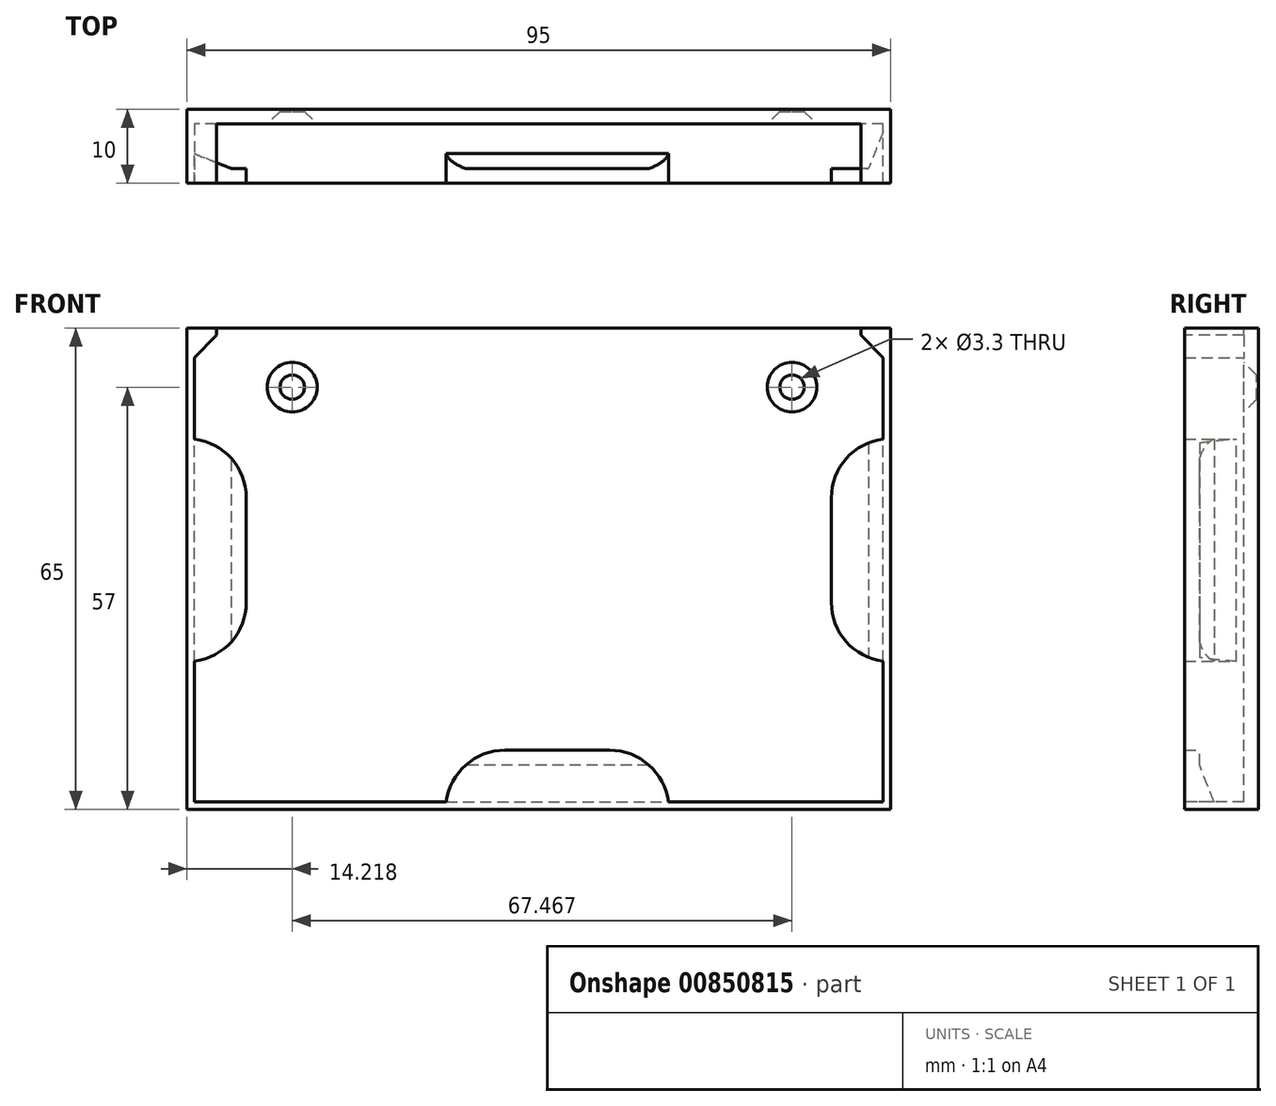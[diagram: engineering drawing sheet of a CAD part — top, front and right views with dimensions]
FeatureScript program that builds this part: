
annotation { "Feature Type Name" : "Feature", "Feature Type Description" : "" }
export const myFeature = defineFeature(function(context is Context, id is Id, definition is map)
    precondition{}
    {
        {
            var Q0;
            Q0=qCreatedBy(makeId("Front.planeOp"),FACE);
            var sketch = newSketch(context, id + "F0", { "sketchPlane" : qUnion([Q0])});
            skPoint(sketch, "E0.middle", {"position": v(0, 0) * mm});
            skLineSegment(sketch, "E1.bottom", {"start": v(47.5, -32.5) * mm, "end": v(-47.5, -32.5) * mm});
            skLineSegment(sketch, "E1.top", {"start": v(47.5, 32.5) * mm, "end": v(-47.5, 32.5) * mm});
            skLineSegment(sketch, "E1.left", {"start": v(47.5, -32.5) * mm, "end": v(47.5, 32.5) * mm});
            skLineSegment(sketch, "E1.right", {"start": v(-47.5, -32.5) * mm, "end": v(-47.5, 32.5) * mm});
            skSolve(sketch);
        }
        {
            var Q0;
            Q0 = qSketchRegion(id + "F0", true);
            extrude(context, id + "F1", {"entities" : qUnion([Q0]), "depth" : 10 * mm, "offsetDistance" : 25 * mm});
        }
        {
            var Q0;
            Q0=makeQuery(id+"F1.opExtrude","CAP_FACE",FACE,{"disambiguationData":[OSD([sQuery(id+"F0.wireOp",EDGE,"E1.bottom"),sQuery(id+"F0.wireOp",EDGE,"E1.top"),sQuery(id+"F0.wireOp",EDGE,"E1.left"),sQuery(id+"F0.wireOp",EDGE,"E1.right")])],"isStart":false});
            var sketch = newSketch(context, id + "F2", { "sketchPlane" : qUnion([Q0])});
            skLineSegment(sketch, "E2.bottom", {"start": v(46.5, -31.5) * mm, "end": v(-46.5, -31.5) * mm});
            skLineSegment(sketch, "E2.top", {"start": v(46.5, 31.5) * mm, "end": v(-46.5, 31.5) * mm});
            skLineSegment(sketch, "E2.left", {"start": v(46.5, -31.5) * mm, "end": v(46.5, 31.5) * mm});
            skLineSegment(sketch, "E2.right", {"start": v(-46.5, -31.5) * mm, "end": v(-46.5, 31.5) * mm});
            skPoint(sketch, "E2.middle", {"position": v(0, 0) * mm});
            skSolve(sketch);
        }
        {
            var Q0;
            Q0 = qSketchRegion(id + "F2", true);
            extrude(context, id + "F3", {"entities" : qUnion([Q0]), "operationType" : NewBodyOperationType.REMOVE, "oppositeDirection" : true, "depth" : 8 * mm, "offsetDistance" : 25 * mm});
        }
        {
            var Q0;
            Q0=makeQuery(id+"F2.imprint","IMPRINT",FACE,{"disambiguationData":[TD([[makeQuery(id+"F2.imprint","IMPRINT",EDGE,{"derivedFrom":sQuery(id+"F2.wireOp",EDGE,"E2.bottom")}),1.0]])]});
            var sketch = newSketch(context, id + "F4", { "sketchPlane" : qUnion([Q0])});
            skLineSegment(sketch, "E3.bottom", {"start": v(-47.5, 17.5) * mm, "end": v(-39.5, 17.5) * mm});
            skLineSegment(sketch, "E3.top", {"start": v(-47.5, -12.5) * mm, "end": v(-39.5, -12.5) * mm});
            skLineSegment(sketch, "E3.left", {"start": v(-47.5, 17.5) * mm, "end": v(-47.5, -12.5) * mm});
            skLineSegment(sketch, "E3.right", {"start": v(-39.5, 17.5) * mm, "end": v(-39.5, -12.5) * mm});
            skLineSegment(sketch, "E4.bottom", {"start": v(39.5, 17.5) * mm, "end": v(47.5, 17.5) * mm});
            skLineSegment(sketch, "E4.top", {"start": v(39.5, -12.5) * mm, "end": v(47.5, -12.5) * mm});
            skLineSegment(sketch, "E4.left", {"start": v(39.5, 17.5) * mm, "end": v(39.5, -12.5) * mm});
            skLineSegment(sketch, "E4.right", {"start": v(47.5, 17.5) * mm, "end": v(47.5, -12.5) * mm});
            skLineSegment(sketch, "E5.bottom", {"start": v(-12.5, -24.5) * mm, "end": v(17.5, -24.5) * mm});
            skLineSegment(sketch, "E5.top", {"start": v(-12.5, -32.5) * mm, "end": v(17.5, -32.5) * mm});
            skLineSegment(sketch, "E5.left", {"start": v(-12.5, -24.5) * mm, "end": v(-12.5, -32.5) * mm});
            skLineSegment(sketch, "E5.right", {"start": v(17.5, -24.5) * mm, "end": v(17.5, -32.5) * mm});
            skSolve(sketch);
        }
        {
            var Q0;
            Q0 = qSketchRegion(id + "F4", true);
            extrude(context, id + "F5", {"entities" : qUnion([Q0]), "operationType" : NewBodyOperationType.ADD, "oppositeDirection" : true, "depth" : 2 * mm, "offsetDistance" : 25 * mm});
        }
        {
            var Q0;
            Q0=makeQuery(id+"F5.opExtrude","SWEPT_EDGE",EDGE,{"disambiguationData":[OSD([sQuery(id+"F4.wireOp",EDGE,"E3.top"),sQuery(id+"F4.wireOp",EDGE,"E3.right")])]});
            var Q1;
            Q1=makeQuery(id+"F5.opExtrude","SWEPT_EDGE",EDGE,{"disambiguationData":[OSD([sQuery(id+"F4.wireOp",EDGE,"E3.bottom"),sQuery(id+"F4.wireOp",EDGE,"E3.right")])]});
            var Q2;
            Q2=makeQuery(id+"F5.opExtrude","SWEPT_EDGE",EDGE,{"disambiguationData":[OSD([sQuery(id+"F4.wireOp",EDGE,"E5.bottom"),sQuery(id+"F4.wireOp",EDGE,"E5.left")])]});
            var Q3;
            Q3=makeQuery(id+"F5.opExtrude","SWEPT_EDGE",EDGE,{"disambiguationData":[OSD([sQuery(id+"F4.wireOp",EDGE,"E5.bottom"),sQuery(id+"F4.wireOp",EDGE,"E5.right")])]});
            var Q4;
            Q4=makeQuery(id+"F5.opExtrude","SWEPT_EDGE",EDGE,{"disambiguationData":[OSD([sQuery(id+"F4.wireOp",EDGE,"E4.bottom"),sQuery(id+"F4.wireOp",EDGE,"E4.left")])]});
            var Q5;
            Q5=makeQuery(id+"F5.opExtrude","SWEPT_EDGE",EDGE,{"disambiguationData":[OSD([sQuery(id+"F4.wireOp",EDGE,"E4.top"),sQuery(id+"F4.wireOp",EDGE,"E4.left")])]});
            fillet(context, id + "F6", {"entities" : qUnion([Q0, Q1, Q2, Q3, Q4, Q5]), "radius" : 8 * mm, "tangentPropagation" : true, "allowEdgeOverflow" : false});
        }
        {
            var Q0;
            Q0=makeQuery(id+"F5.boolean.opBoolean","INTERSECT",EDGE,{"derivedFrom":[makeQuery(id+"F3.boolean.opBoolean","COPY",FACE,{"derivedFrom":makeQuery(id+"F3.opExtrude","SWEPT_FACE",FACE,{"disambiguationData":[OSD([sQuery(id+"F2.wireOp",EDGE,"E2.right")])]})}),makeQuery(id+"F5.opExtrude","CAP_FACE",FACE,{"disambiguationData":[OSD([sQuery(id+"F4.wireOp",EDGE,"E3.bottom"),sQuery(id+"F4.wireOp",EDGE,"E3.top"),sQuery(id+"F4.wireOp",EDGE,"E3.left"),sQuery(id+"F4.wireOp",EDGE,"E3.right")])],"isStart":false})]});
            var Q1;
            Q1=makeQuery(id+"F5.boolean.opBoolean","INTERSECT",EDGE,{"derivedFrom":[makeQuery(id+"F3.boolean.opBoolean","COPY",FACE,{"derivedFrom":makeQuery(id+"F3.opExtrude","SWEPT_FACE",FACE,{"disambiguationData":[OSD([sQuery(id+"F2.wireOp",EDGE,"E2.left")])]})}),makeQuery(id+"F5.opExtrude","CAP_FACE",FACE,{"disambiguationData":[OSD([sQuery(id+"F4.wireOp",EDGE,"E4.bottom"),sQuery(id+"F4.wireOp",EDGE,"E4.top"),sQuery(id+"F4.wireOp",EDGE,"E4.left"),sQuery(id+"F4.wireOp",EDGE,"E4.right")])],"isStart":false})]});
            var Q2;
            Q2=makeQuery(id+"F5.boolean.opBoolean","INTERSECT",EDGE,{"derivedFrom":[makeQuery(id+"F3.boolean.opBoolean","COPY",FACE,{"derivedFrom":makeQuery(id+"F3.opExtrude","SWEPT_FACE",FACE,{"disambiguationData":[OSD([sQuery(id+"F2.wireOp",EDGE,"E2.bottom")])]})}),makeQuery(id+"F5.opExtrude","CAP_FACE",FACE,{"disambiguationData":[OSD([sQuery(id+"F4.wireOp",EDGE,"E5.bottom"),sQuery(id+"F4.wireOp",EDGE,"E5.top"),sQuery(id+"F4.wireOp",EDGE,"E5.left"),sQuery(id+"F4.wireOp",EDGE,"E5.right")])],"isStart":false})]});
            chamfer(context, id + "F7", {"entities" : qUnion([Q0, Q1, Q2]), "chamferType" : ChamferType.TWO_OFFSETS, "width1" : 2 * mm, "oppositeDirection" : false, "width2" : 5 * mm, "tangentPropagation" : true});
        }
        {
            var Q0;
            Q0=makeQuery(id+"F1.opExtrude","SWEPT_FACE",FACE,{"disambiguationData":[OSD([sQuery(id+"F0.wireOp",EDGE,"E1.top")])]});
            var sketch = newSketch(context, id + "F8", { "sketchPlane" : qUnion([Q0])});
            skLineSegment(sketch, "E6.bottom", {"start": v(43.5, -2) * mm, "end": v(-43.5, -2) * mm});
            skLineSegment(sketch, "E6.top", {"start": v(43.5, -18) * mm, "end": v(-43.5, -18) * mm});
            skLineSegment(sketch, "E6.left", {"start": v(43.5, -2) * mm, "end": v(43.5, -18) * mm});
            skLineSegment(sketch, "E6.right", {"start": v(-43.5, -2) * mm, "end": v(-43.5, -18) * mm});
            skPoint(sketch, "E6.middle", {"position": v(0, -10) * mm});
            skSolve(sketch);
        }
        {
            var Q0;
            {var subQ0=sQuery(id+"F8.wireOp",EDGE,"E6.bottom");Q0=makeQuery(id+"F8.imprint","IMPRINT",FACE,{"disambiguationData":[TD([[makeQuery(id+"F8.imprint","IMPRINT",EDGE,{"derivedFrom":subQ0}),1.0]])]});}
            extrude(context, id + "F9", {"entities" : qUnion([Q0]), "operationType" : NewBodyOperationType.REMOVE, "oppositeDirection" : true, "depth" : 10 * mm, "offsetDistance" : 25 * mm});
        }
        {
            var Q0;
            Q0=makeQuery(id+"F3.boolean.opBoolean","COPY",EDGE,{"derivedFrom":makeQuery(id+"F3.opExtrude","SWEPT_EDGE",EDGE,{"disambiguationData":[OSD([sQuery(id+"F2.wireOp",EDGE,"E2.top"),sQuery(id+"F2.wireOp",EDGE,"E2.right")])]})});
            var Q1;
            Q1=makeQuery(id+"F3.boolean.opBoolean","COPY",EDGE,{"derivedFrom":makeQuery(id+"F3.opExtrude","SWEPT_EDGE",EDGE,{"disambiguationData":[OSD([sQuery(id+"F2.wireOp",EDGE,"E2.top"),sQuery(id+"F2.wireOp",EDGE,"E2.left")])]})});
            chamfer(context, id + "F10", {"entities" : qUnion([Q0, Q1]), "width" : 3 * mm, "tangentPropagation" : true});
        }
        {
            var Q0;
            Q0=makeQuery(id+"F9.boolean.opBoolean","MERGE",FACE,{"derivedFrom":[makeQuery(id+"F3.boolean.opBoolean","COPY",FACE,{"derivedFrom":makeQuery(id+"F3.opExtrude","CAP_FACE",FACE,{"disambiguationData":[OSD([sQuery(id+"F2.wireOp",EDGE,"E2.bottom"),sQuery(id+"F2.wireOp",EDGE,"E2.top"),sQuery(id+"F2.wireOp",EDGE,"E2.left"),sQuery(id+"F2.wireOp",EDGE,"E2.right")])],"isStart":false})}),makeQuery(id+"F9.opExtrude","SWEPT_FACE",FACE,{"disambiguationData":[OSD([sQuery(id+"F8.wireOp",EDGE,"E6.bottom")])]})]});
            var sketch = newSketch(context, id + "F11", { "sketchPlane" : qUnion([Q0])});
            skPoint(sketch, "E7", {"position": v(34.19, 24.5) * mm});
            skPoint(sketch, "E8", {"position": v(-33.28, 24.5) * mm});
            skSolve(sketch);
        }
        {
            var Q0;
            Q0=sQuery(id+"F11.wireOp",VERTEX,"E7");
            var Q1;
            Q1=sQuery(id+"F11.wireOp",VERTEX,"E8");
            var Q2;
            Q2=makeQuery(id+"F1.opExtrude","SWEPT_BODY",BODY,{"disambiguationData":[OSD([sQuery(id+"F0.wireOp",EDGE,"E1.bottom"),sQuery(id+"F0.wireOp",EDGE,"E1.top"),sQuery(id+"F0.wireOp",EDGE,"E1.left"),sQuery(id+"F0.wireOp",EDGE,"E1.right")])]});
            hole(context, id + "F12", {"style" : HoleStyle.C_SINK, "endStyle" : HoleEndStyle.THROUGH, "standardTappedOrClearance" : lookupTablePath({ "fit" : "Normal", "standard" : "ISO", "size" : "M3", "type" : "Clearance" }), "standardBlindInLast" : lookupTablePath({ "fit" : "Standard", "standard" : "ISO", "size" : "M3", "type" : "Clearance" }), "holeDiameter" : 3.3 * mm, "cSinkDiameter" : 6.72 * mm, "cSinkAngle" : 90 * degree, "majorDiameter" : 5 * mm, "isTappedThrough" : true, "tappedDepth" : 8 * mm, "tapClearance" : 3, "startFromSketch" : true, "locations" : qUnion([Q0, Q1]), "scope" : qUnion([Q2])});
        }
    });
